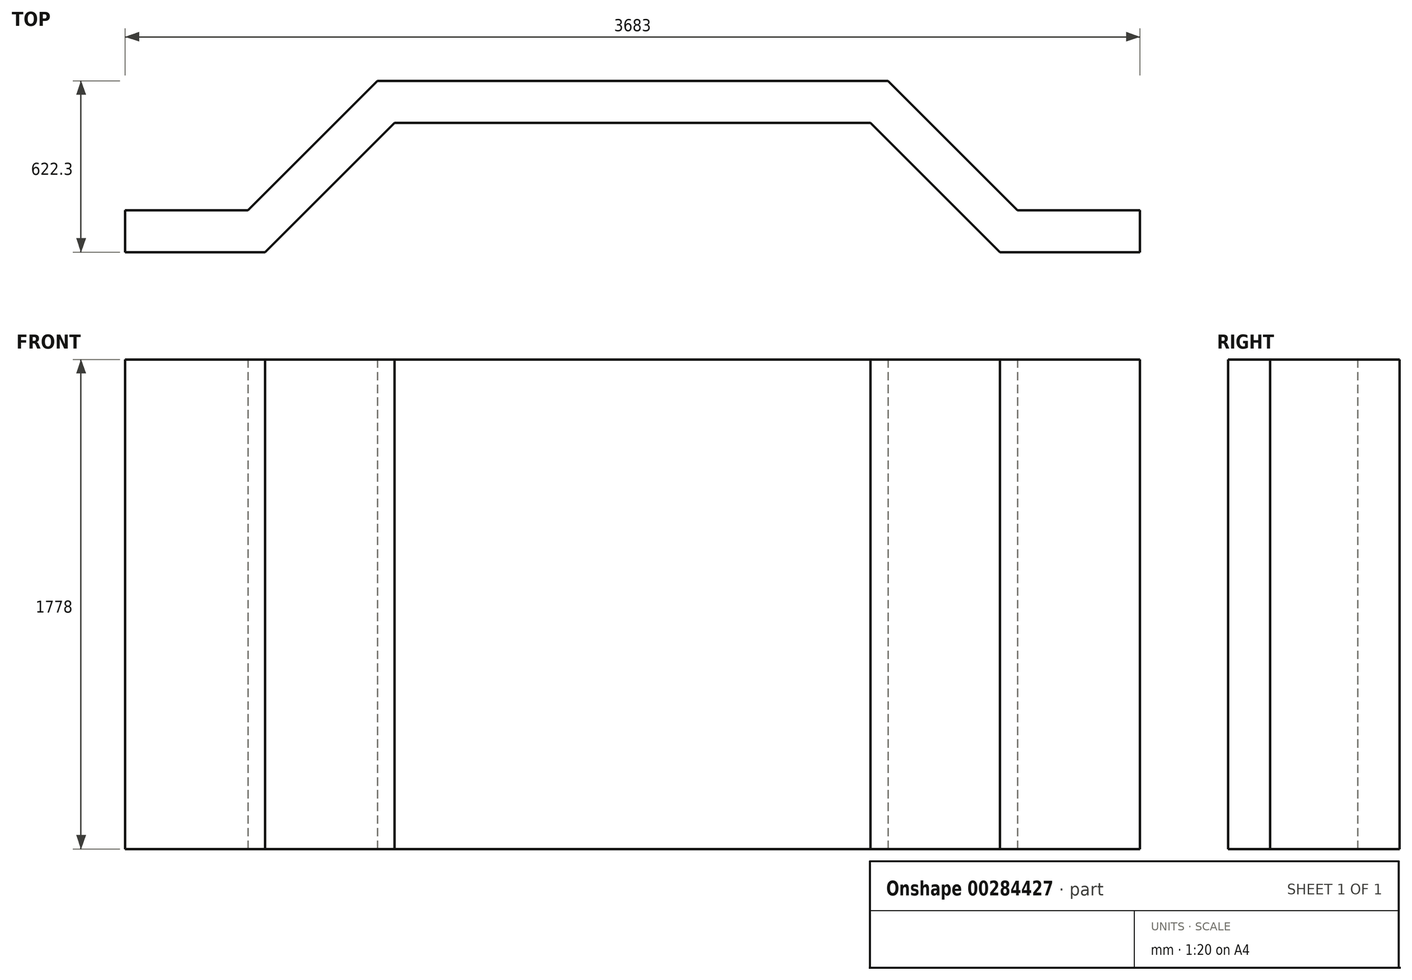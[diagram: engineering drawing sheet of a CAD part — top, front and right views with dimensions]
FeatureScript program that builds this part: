
annotation { "Feature Type Name" : "Feature", "Feature Type Description" : "" }
export const myFeature = defineFeature(function(context is Context, id is Id, definition is map)
    precondition{}
    {
        {
            var Q0;
            Q0=qCreatedBy(makeId("Top.planeOp"),FACE);
            var sketch = newSketch(context, id + "F0", { "sketchPlane" : qUnion([Q0])});
            skLineSegment(sketch, "E0", {"start": v(0, 0) * mm, "end": v(-863.6, 0) * mm});
            skLineSegment(sketch, "E1", {"start": v(-863.6, 0) * mm, "end": v(-1333.5, -469.9) * mm});
            skLineSegment(sketch, "E2", {"start": v(-1333.5, -469.9) * mm, "end": v(-1841.5, -469.9) * mm});
            skLineSegment(sketch, "E3", {"start": v(-1841.5, -469.9) * mm, "end": v(-1841.5, -317.5) * mm});
            skLineSegment(sketch, "E4", {"start": v(-1841.5, -317.5) * mm, "end": v(-1396.63, -317.5) * mm});
            skLineSegment(sketch, "E5", {"start": v(-1396.63, -317.5) * mm, "end": v(-926.73, 152.4) * mm});
            skLineSegment(sketch, "E6", {"start": v(-926.73, 152.4) * mm, "end": v(0, 152.4) * mm});
            skLineSegment(sketch, "E7.MirrorCS", {"start": v(926.73, 152.4) * mm, "end": v(0, 152.4) * mm});
            skLineSegment(sketch, "E8.MirrorCS", {"start": v(1333.5, -469.9) * mm, "end": v(1841.5, -469.9) * mm});
            skLineSegment(sketch, "E9.MirrorCS", {"start": v(1841.5, -469.9) * mm, "end": v(1841.5, -317.5) * mm});
            skLineSegment(sketch, "E10.MirrorCS", {"start": v(1841.5, -317.5) * mm, "end": v(1396.63, -317.5) * mm});
            skLineSegment(sketch, "E11.MirrorCS", {"start": v(1396.63, -317.5) * mm, "end": v(926.73, 152.4) * mm});
            skLineSegment(sketch, "E12.MirrorCS", {"start": v(863.6, 0) * mm, "end": v(1333.5, -469.9) * mm});
            skLineSegment(sketch, "E13.MirrorCS", {"start": v(0, 0) * mm, "end": v(863.6, 0) * mm});
            skSolve(sketch);
        }
        {
            var Q0;
            Q0=makeQuery(id+"F0.imprint","IMPRINT",FACE,{"disambiguationData":[TD([[makeQuery(id+"F0.imprint","IMPRINT",EDGE,{"derivedFrom":sQuery(id+"F0.wireOp",EDGE,"E0")}),-1.0]])]});
            extrude(context, id + "F1", {"entities" : qUnion([Q0]), "depth" : 1778 * mm, "offsetDistance" : 25.4 * mm});
        }
    });
